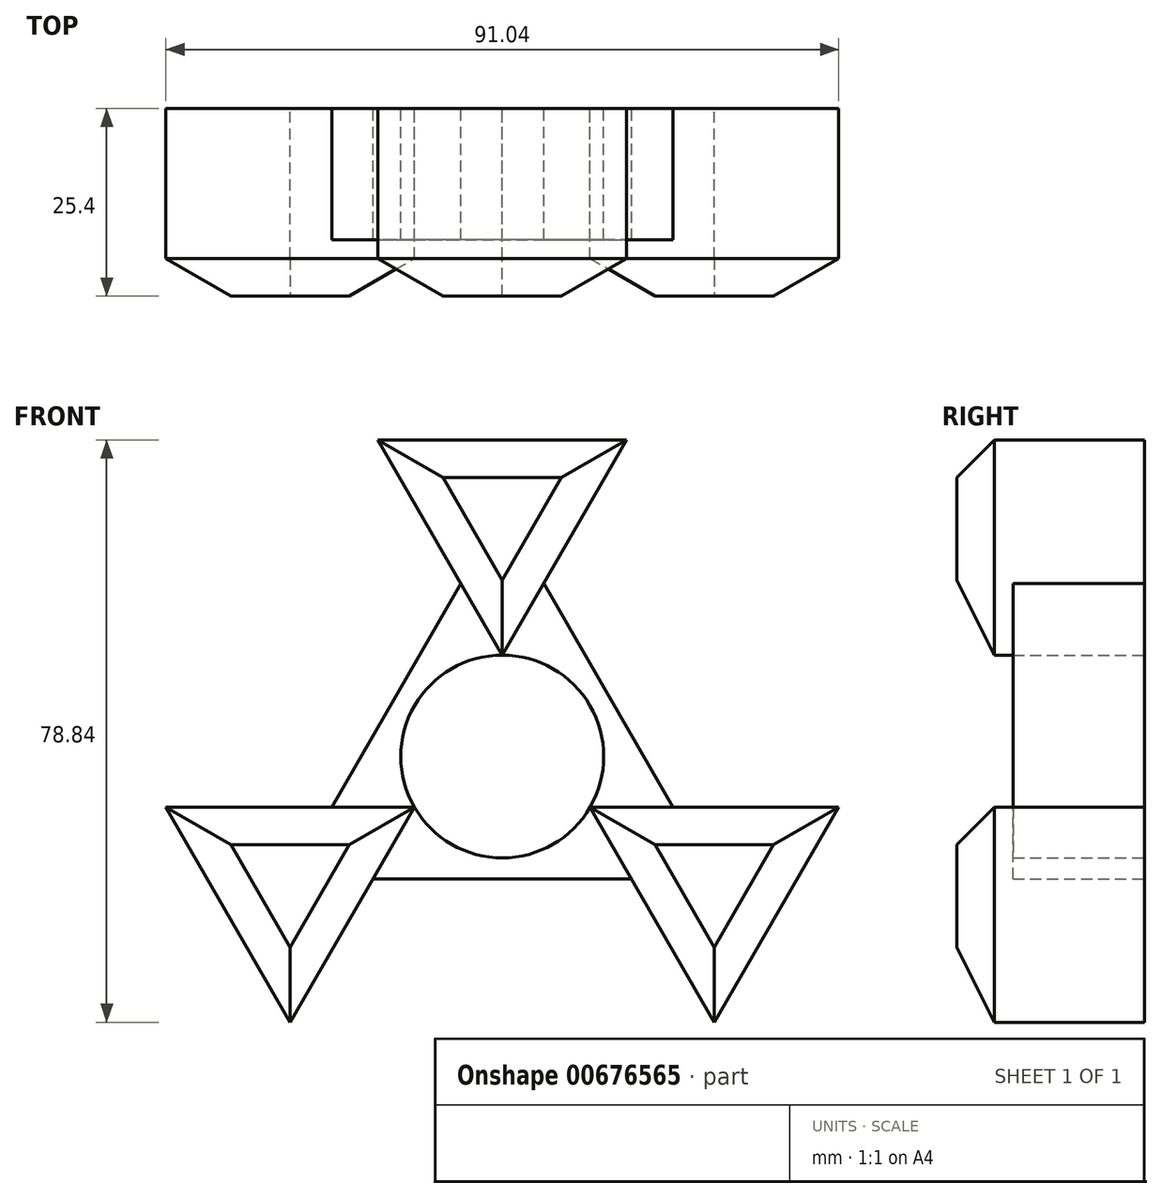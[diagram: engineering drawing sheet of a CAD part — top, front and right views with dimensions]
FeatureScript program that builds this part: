
annotation { "Feature Type Name" : "Feature", "Feature Type Description" : "" }
export const myFeature = defineFeature(function(context is Context, id is Id, definition is map)
    precondition{}
    {
        {
            var Q0;
            Q0=qCreatedBy(makeId("Front.planeOp"),FACE);
            var sketch = newSketch(context, id + "F0", { "sketchPlane" : qUnion([Q0])});
            skCircle(sketch, "E0.cCircle", {"center": v(0, 0) * mm, "radius": 33.14 * mm, "construction": true});
            skLineSegment(sketch, "E0.0", {"start": v(0, 33.14) * mm, "end": v(28.7, -16.57) * mm});
            skLineSegment(sketch, "E0.1", {"start": v(28.7, -16.57) * mm, "end": v(-28.7, -16.57) * mm});
            skLineSegment(sketch, "E0.2", {"start": v(-28.7, -16.57) * mm, "end": v(0, 33.14) * mm});
            skLineSegment(sketch, "E1", {"start": v(0, 0) * mm, "end": v(0, 33.14) * mm});
            skLineSegment(sketch, "E2", {"start": v(0, 0) * mm, "end": v(-28.7, -16.57) * mm});
            skLineSegment(sketch, "E3", {"start": v(0, 0) * mm, "end": v(28.7, -16.57) * mm});
            skCircle(sketch, "E4", {"center": v(0, 0) * mm, "radius": 13.73 * mm});
            skCircle(sketch, "E5.cCircle", {"center": v(28.7, -16.57) * mm, "radius": 19.41 * mm, "construction": true});
            skLineSegment(sketch, "E5.0", {"start": v(11.89, -6.86) * mm, "end": v(45.52, -6.86) * mm});
            skLineSegment(sketch, "E5.1", {"start": v(45.52, -6.86) * mm, "end": v(28.7, -35.99) * mm});
            skLineSegment(sketch, "E5.2", {"start": v(28.7, -35.99) * mm, "end": v(11.89, -6.86) * mm});
            skCircle(sketch, "E6.cCircle", {"center": v(0, 33.14) * mm, "radius": 19.41 * mm, "construction": true});
            skPoint(sketch, "E6.cCircle.perimeterSnap0", {"position": v(0, 16.57) * mm});
            skLineSegment(sketch, "E6.0", {"start": v(0, 13.73) * mm, "end": v(-16.81, 42.85) * mm});
            skPoint(sketch, "E6.0.startSnap0", {"position": v(0, 16.57) * mm});
            skLineSegment(sketch, "E6.1", {"start": v(-16.81, 42.85) * mm, "end": v(16.81, 42.85) * mm});
            skLineSegment(sketch, "E6.2", {"start": v(16.81, 42.85) * mm, "end": v(0, 13.73) * mm});
            skCircle(sketch, "E7.cCircle", {"center": v(-28.7, -16.57) * mm, "radius": 19.41 * mm, "construction": true});
            skLineSegment(sketch, "E7.0", {"start": v(-11.89, -6.86) * mm, "end": v(-28.7, -35.99) * mm});
            skLineSegment(sketch, "E7.1", {"start": v(-28.7, -35.99) * mm, "end": v(-45.52, -6.86) * mm});
            skLineSegment(sketch, "E7.2", {"start": v(-45.52, -6.86) * mm, "end": v(-11.89, -6.86) * mm});
            skSolve(sketch);
        }
        {
            var Q0;
            {var subQ0=sQuery(id+"F0.wireOp",EDGE,"E5.1");Q0=makeQuery(id+"F0.imprint","IMPRINT",FACE,{"disambiguationData":[TD([[makeQuery(id+"F0.imprint","IMPRINT",EDGE,{"derivedFrom":subQ0}),-1.0]])]});}
            var Q1;
            {var subQ1=sQuery(id+"F0.wireOp",EDGE,"E0.0");var subQ3=sQuery(id+"F0.wireOp",EDGE,"E5.0");var subQ4=makeQuery(id+"F0.imprint","INTERSECT",VERTEX,{"derivedFrom":[subQ1,subQ3]});Q1=makeQuery(id+"F0.imprint","IMPRINT",FACE,{"disambiguationData":[TD([[makeQuery(id+"F0.imprint","IMPRINT",EDGE,{"disambiguationData":[TD([[subQ4,-1.0]])],"derivedFrom":subQ1}),-1.0]])]});}
            var Q2;
            {var subQ1=sQuery(id+"F0.wireOp",EDGE,"E0.1");var subQ3=sQuery(id+"F0.wireOp",EDGE,"E5.2");var subQ4=makeQuery(id+"F0.imprint","INTERSECT",VERTEX,{"derivedFrom":[subQ1,subQ3]});Q2=makeQuery(id+"F0.imprint","IMPRINT",FACE,{"disambiguationData":[TD([[makeQuery(id+"F0.imprint","IMPRINT",EDGE,{"disambiguationData":[TD([[subQ4,1.0]])],"derivedFrom":subQ1}),-1.0]])]});}
            var Q3;
            {var subQ0=sQuery(id+"F0.wireOp",EDGE,"E7.1");Q3=makeQuery(id+"F0.imprint","IMPRINT",FACE,{"disambiguationData":[TD([[makeQuery(id+"F0.imprint","IMPRINT",EDGE,{"derivedFrom":subQ0}),-1.0]])]});}
            var Q4;
            {var subQ1=sQuery(id+"F0.wireOp",EDGE,"E0.2");var subQ3=sQuery(id+"F0.wireOp",EDGE,"E7.2");var subQ4=makeQuery(id+"F0.imprint","INTERSECT",VERTEX,{"derivedFrom":[subQ1,subQ3]});Q4=makeQuery(id+"F0.imprint","IMPRINT",FACE,{"disambiguationData":[TD([[makeQuery(id+"F0.imprint","IMPRINT",EDGE,{"disambiguationData":[TD([[subQ4,1.0]])],"derivedFrom":subQ1}),-1.0]])]});}
            var Q5;
            {var subQ1=sQuery(id+"F0.wireOp",EDGE,"E0.1");var subQ3=sQuery(id+"F0.wireOp",EDGE,"E7.0");var subQ4=makeQuery(id+"F0.imprint","INTERSECT",VERTEX,{"derivedFrom":[subQ1,subQ3]});Q5=makeQuery(id+"F0.imprint","IMPRINT",FACE,{"disambiguationData":[TD([[makeQuery(id+"F0.imprint","IMPRINT",EDGE,{"disambiguationData":[TD([[subQ4,-1.0]])],"derivedFrom":subQ1}),-1.0]])]});}
            var Q6;
            {var subQ1=sQuery(id+"F0.wireOp",EDGE,"E0.0");var subQ3=sQuery(id+"F0.wireOp",EDGE,"E6.2");var subQ4=makeQuery(id+"F0.imprint","INTERSECT",VERTEX,{"derivedFrom":[subQ1,subQ3]});Q6=makeQuery(id+"F0.imprint","IMPRINT",FACE,{"disambiguationData":[TD([[makeQuery(id+"F0.imprint","IMPRINT",EDGE,{"disambiguationData":[TD([[subQ4,1.0]])],"derivedFrom":subQ1}),-1.0]])]});}
            var Q7;
            {var subQ1=sQuery(id+"F0.wireOp",EDGE,"E0.2");var subQ3=sQuery(id+"F0.wireOp",EDGE,"E6.0");var subQ4=makeQuery(id+"F0.imprint","INTERSECT",VERTEX,{"derivedFrom":[subQ1,subQ3]});Q7=makeQuery(id+"F0.imprint","IMPRINT",FACE,{"disambiguationData":[TD([[makeQuery(id+"F0.imprint","IMPRINT",EDGE,{"disambiguationData":[TD([[subQ4,-1.0]])],"derivedFrom":subQ1}),-1.0]])]});}
            var Q8;
            {var subQ0=sQuery(id+"F0.wireOp",EDGE,"E6.1");Q8=makeQuery(id+"F0.imprint","IMPRINT",FACE,{"disambiguationData":[TD([[makeQuery(id+"F0.imprint","IMPRINT",EDGE,{"derivedFrom":subQ0}),-1.0]])]});}
            extrude(context, id + "F1", {"entities" : qUnion([Q0, Q1, Q2, Q3, Q4, Q5, Q6, Q7, Q8]), "depth" : 25.4 * mm, "offsetDistance" : 25.4 * mm});
        }
        {
            var Q0;
            {var subQ0=sQuery(id+"F0.wireOp",EDGE,"E6.2");var subQ1=sQuery(id+"F0.wireOp",EDGE,"E0.0");var subQ2=makeQuery(id+"F0.imprint","INTERSECT",VERTEX,{"derivedFrom":[subQ1,subQ0]});Q0=makeQuery(id+"F0.imprint","IMPRINT",FACE,{"disambiguationData":[TD([[makeQuery(id+"F0.imprint","IMPRINT",EDGE,{"disambiguationData":[TD([[subQ2,-1.0]])],"derivedFrom":subQ1}),-1.0]])]});}
            var Q1;
            {var subQ0=sQuery(id+"F0.wireOp",EDGE,"E5.2");var subQ1=sQuery(id+"F0.wireOp",EDGE,"E0.1");var subQ2=makeQuery(id+"F0.imprint","INTERSECT",VERTEX,{"derivedFrom":[subQ1,subQ0]});Q1=makeQuery(id+"F0.imprint","IMPRINT",FACE,{"disambiguationData":[TD([[makeQuery(id+"F0.imprint","IMPRINT",EDGE,{"disambiguationData":[TD([[subQ2,-1.0]])],"derivedFrom":subQ1}),-1.0]])]});}
            var Q2;
            {var subQ0=sQuery(id+"F0.wireOp",EDGE,"E7.2");var subQ1=sQuery(id+"F0.wireOp",EDGE,"E0.2");var subQ2=makeQuery(id+"F0.imprint","INTERSECT",VERTEX,{"derivedFrom":[subQ1,subQ0]});Q2=makeQuery(id+"F0.imprint","IMPRINT",FACE,{"disambiguationData":[TD([[makeQuery(id+"F0.imprint","IMPRINT",EDGE,{"disambiguationData":[TD([[subQ2,-1.0]])],"derivedFrom":subQ1}),-1.0]])]});}
            extrude(context, id + "F2", {"entities" : qUnion([Q0, Q1, Q2]), "depth" : 17.78 * mm, "offsetDistance" : 25.4 * mm});
        }
        {
            var Q0;
            Q0=makeQuery(id+"F1.opExtrude","CAP_EDGE",EDGE,{"disambiguationData":[OSD([sQuery(id+"F0.wireOp",EDGE,"E6.0")])],"isStart":false});
            var Q1;
            Q1=makeQuery(id+"F1.opExtrude","CAP_EDGE",EDGE,{"disambiguationData":[OSD([sQuery(id+"F0.wireOp",EDGE,"E6.2")])],"isStart":false});
            var Q2;
            Q2=makeQuery(id+"F1.opExtrude","CAP_EDGE",EDGE,{"disambiguationData":[OSD([sQuery(id+"F0.wireOp",EDGE,"E5.0")])],"isStart":false});
            var Q3;
            Q3=makeQuery(id+"F1.opExtrude","CAP_EDGE",EDGE,{"disambiguationData":[OSD([sQuery(id+"F0.wireOp",EDGE,"E5.2")])],"isStart":false});
            var Q4;
            Q4=makeQuery(id+"F1.opExtrude","CAP_EDGE",EDGE,{"disambiguationData":[OSD([sQuery(id+"F0.wireOp",EDGE,"E7.0")])],"isStart":false});
            var Q5;
            Q5=makeQuery(id+"F1.opExtrude","CAP_EDGE",EDGE,{"disambiguationData":[OSD([sQuery(id+"F0.wireOp",EDGE,"E7.2")])],"isStart":false});
            var Q6;
            Q6=makeQuery(id+"F1.opExtrude","CAP_EDGE",EDGE,{"disambiguationData":[OSD([sQuery(id+"F0.wireOp",EDGE,"E7.1")])],"isStart":false});
            var Q7;
            Q7=makeQuery(id+"F1.opExtrude","CAP_EDGE",EDGE,{"disambiguationData":[OSD([sQuery(id+"F0.wireOp",EDGE,"E6.1")])],"isStart":false});
            chamfer(context, id + "F3", {"entities" : qUnion([Q0, Q1, Q2, Q3, Q4, Q5, Q6, Q7]), "width" : 5.08 * mm, "tangentPropagation" : true});
        }
        {
            var Q0;
            Q0=makeQuery(id+"F1.opExtrude","CAP_EDGE",EDGE,{"disambiguationData":[OSD([sQuery(id+"F0.wireOp",EDGE,"E5.1")])],"isStart":false});
            chamfer(context, id + "F4", {"entities" : qUnion([Q0]), "width" : 5.08 * mm, "tangentPropagation" : true});
        }
    });
